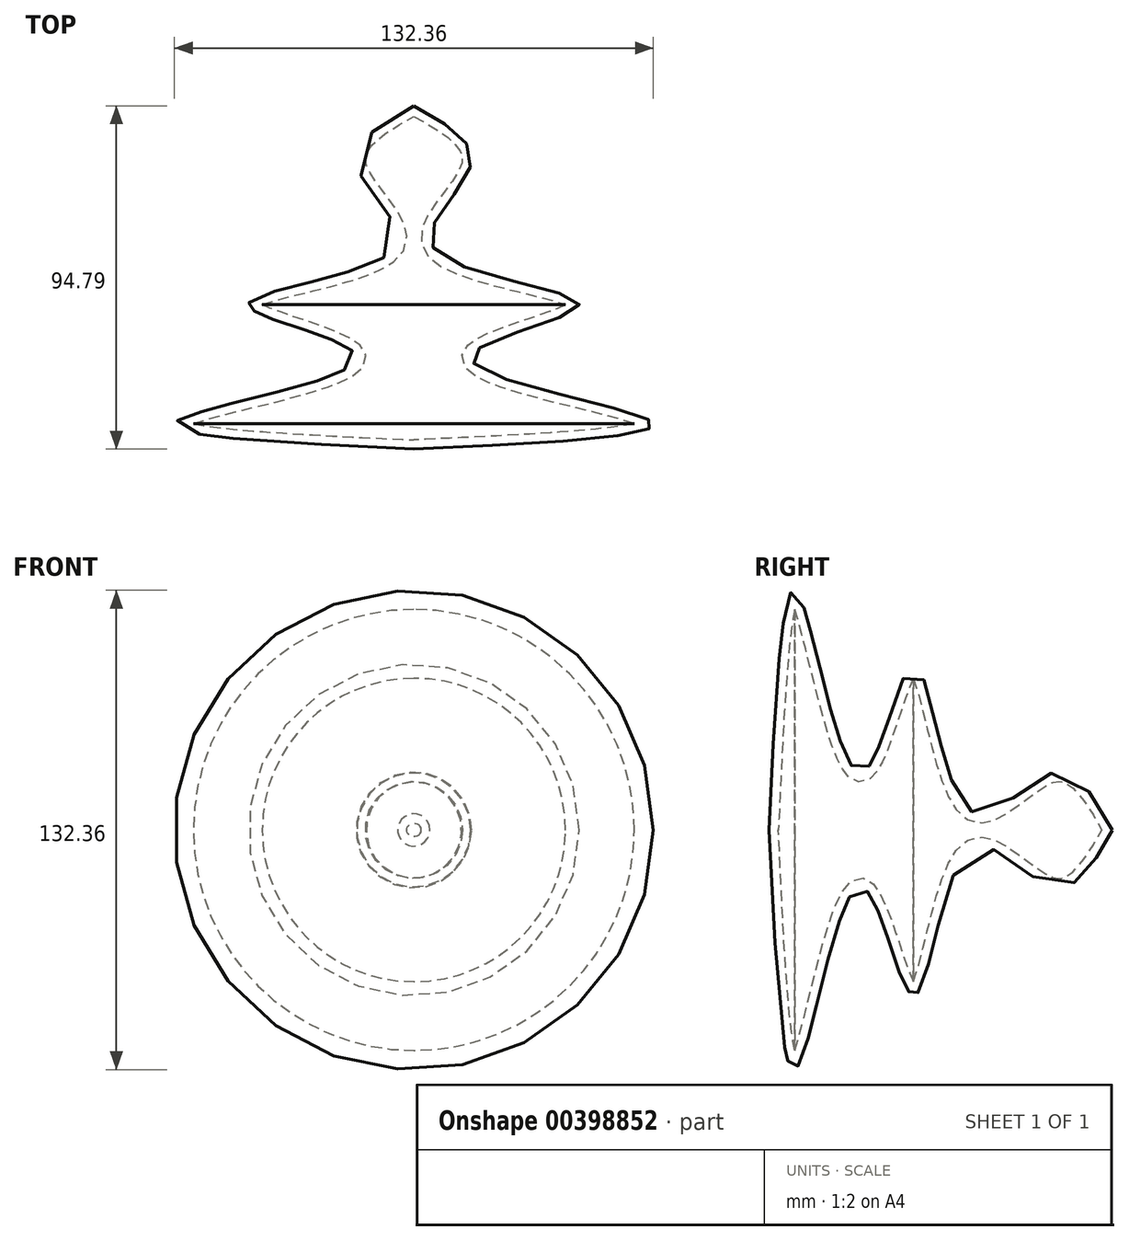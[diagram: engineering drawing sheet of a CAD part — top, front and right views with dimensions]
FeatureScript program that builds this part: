
annotation { "Feature Type Name" : "Feature", "Feature Type Description" : "" }
export const myFeature = defineFeature(function(context is Context, id is Id, definition is map)
    precondition{}
    {
        {
            var Q0;
            Q0=qCreatedBy(makeId("Top.planeOp"),FACE);
            var sketch = newSketch(context, id + "F0", { "sketchPlane" : qUnion([Q0])});
            skLineSegment(sketch, "E0", {"start": v(0, 50.84) * mm, "end": v(0, -43.95) * mm});
            skFitSpline(sketch, "E1", {"points": [v(0, 50.84) * mm, v(15.77, 34.49) * mm, v(5.32, 11.63) * mm, v(45.72, -4.14) * mm, v(15.77, -18.52) * mm, v(65.03, -35.87) * mm, v(0, -43.95) * mm], "startDerivative": vector(204.65, -112.6) * mm, "endDerivative": vector(-507.72, -23.45) * mm});
            skSolve(sketch);
        }
        {
            var Q0;
            Q0=makeQuery(id+"F0.imprint","IMPRINT",FACE,{"disambiguationData":[TD([[makeQuery(id+"F0.imprint","IMPRINT",EDGE,{"derivedFrom":sQuery(id+"F0.wireOp",EDGE,"E0")}),1.0]])]});
            var Q1;
            Q1=sQuery(id+"F0.wireOp",EDGE,"E0");
            revolve(context, id + "F1", {"entities" : qUnion([Q0]), "axis" : qUnion([Q1]), "revolveType" : RevolveType.FULL});
        }
        {
            var Q0;
            Q0=makeQuery(id+"F1.opRevolve","SWEPT_FACE",FACE,{"disambiguationData":[OSD([sQuery(id+"F0.wireOp",EDGE,"E1")])]});
            var Q1;
            Q1=makeQuery(id+"F1.opRevolve","SWEPT_BODY",BODY,{"disambiguationData":[OSD([sQuery(id+"F0.wireOp",EDGE,"E0"),sQuery(id+"F0.wireOp",EDGE,"E1")])]});
            shell(context, id + "F2", {"isHollow" : true, "entities" : qUnion([Q0]), "parts" : qUnion([Q1]), "thickness" : 2.54 * mm});
        }
    });
